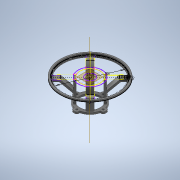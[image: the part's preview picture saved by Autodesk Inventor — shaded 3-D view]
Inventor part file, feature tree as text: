
AUTODESK INVENTOR PART (.ipt)
format: ipt  version: 2020 (Build 240168000, 168)  size: 479,744 bytes
history: native  units: mm
features: projected_geometry x23, sketch x13, extrude x6, other x4, pattern_circular x1, sweep x1
ambient origin geometry x8: Origin, YZ Plane, XZ Plane, XY Plane, X Axis, Y Axis, Z Axis, Center Point
bodies: Body1 (feature_tree)
feature tree (48):
  other  "Твердое тело1"
  extrude  "Выдавливание1"  Depth=44.0mm
  extrude  "Выдавливание2"  Depth=3.0mm
  sketch  "Эскиз3"
  extrude  "Выдавливание4"  Depth=40.0mm TaperAngle=360.0deg
  pattern_circular  "Круговой массив1"  [2 undecoded]
  other  "РабПлоскость2"
  sketch  "Эскиз5"
  other  "РабПлоскость1"
  sketch  "Эскиз6"
  sketch  "Эскиз7"
  extrude  "Выдавливание6"  Depth=4.5mm
  sketch  "Эскиз8"
  extrude  "Выдавливание7"  Depth=3.0mm
  sketch  "Эскиз9"
  other  "РабПлоскость3"
  sketch  "Эскиз10"
  sweep  "Сдвиг1"
  extrude  "Выдавливание8"  Depth=1.0mm
  sketch  "Эскиз1"
  sketch  "Эскиз2"
  sketch  "Эскиз4"
  projected_geometry  "Спроецированная петля1"
  projected_geometry  "Спроецированная петля2"
  projected_geometry  "Спроецированная петля3"
  projected_geometry  "Спроецированная петля4"
  projected_geometry  "Спроецированная петля5"
  projected_geometry  "Спроецированная петля6"
  projected_geometry  "Спроецированная петля7"
  projected_geometry  "Спроецированная петля8"
  projected_geometry  "Спроецированная петля9"
  projected_geometry  "Спроецированная петля10"
  projected_geometry  "Спроецированная петля11"
  projected_geometry  "Спроецированная петля12"
  projected_geometry  "Спроецированная петля13"
  projected_geometry  "Спроецированная петля14"
  projected_geometry  "Спроецированная петля15"
  projected_geometry  "Спроецированная петля16"
  projected_geometry  "Спроецированная петля17"
  projected_geometry  "Спроецированная петля18"
  projected_geometry  "Спроецированная петля19"
  projected_geometry  "Спроецированная петля20"
  sketch  "Эскиз11"
  projected_geometry  "Спроецированная петля21"
  projected_geometry  "Спроецированная петля22"
  projected_geometry  "Спроецированная петля23"
  sketch  "3D эскиз1"
  sketch  "Эскиз12"
note: 2 required parameter values undecoded (feature->parameter linkage not recoverable at this tier; creation-order binding heuristic only, values carry confidence <= 0.55)
